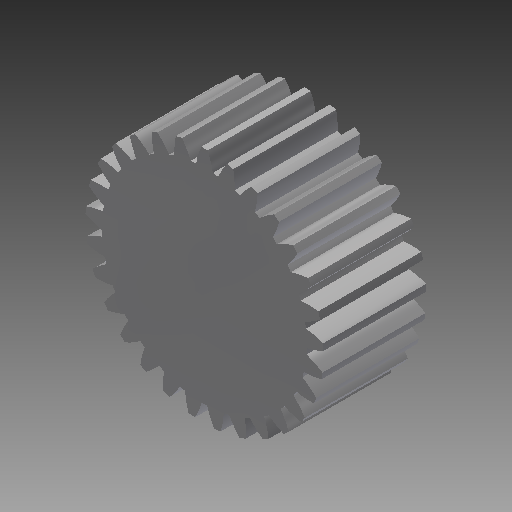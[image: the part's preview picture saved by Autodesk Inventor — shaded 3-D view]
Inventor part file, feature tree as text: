
AUTODESK INVENTOR PART (.ipt)
format: ipt  version: 2019 (Build 230136000, 136)  size: 266,240 bytes
history: native  units: mm (DEFAULTED — no unit token found)
features: plane x3, other x3, sketch x2, extrude x1
ambient origin geometry x8: Origin, YZ Plane, XZ Plane, XY Plane, X Axis, Y Axis, Z Axis, Center Point
bodies: Solid1 (feature_tree)
feature tree (9):
  extrude  "Extrusion1"  Depth=20.0mm TaperAngle=0.0deg
  plane  "Work Plane2"
  plane  "Work Plane8"
  plane  "Work Plane9"
  other  "正齒輪"
  sketch  "Sketch1"  dims[d0=46.224141mm d1=20.0mm d2=0.0mm]
  sketch  "Sketch2"  dims[d3=44.65676mm d4=10.0mm d5=0.0mm d16=57.74581mm d17=0.0mm d34=1.083308mm d39=0.0mm d41=0.0mm d43=57.74581mm d46=57.74581mm d47=0.0mm d48=0.0mm]
  other  "Srf1"
  other  "節圓直徑"
